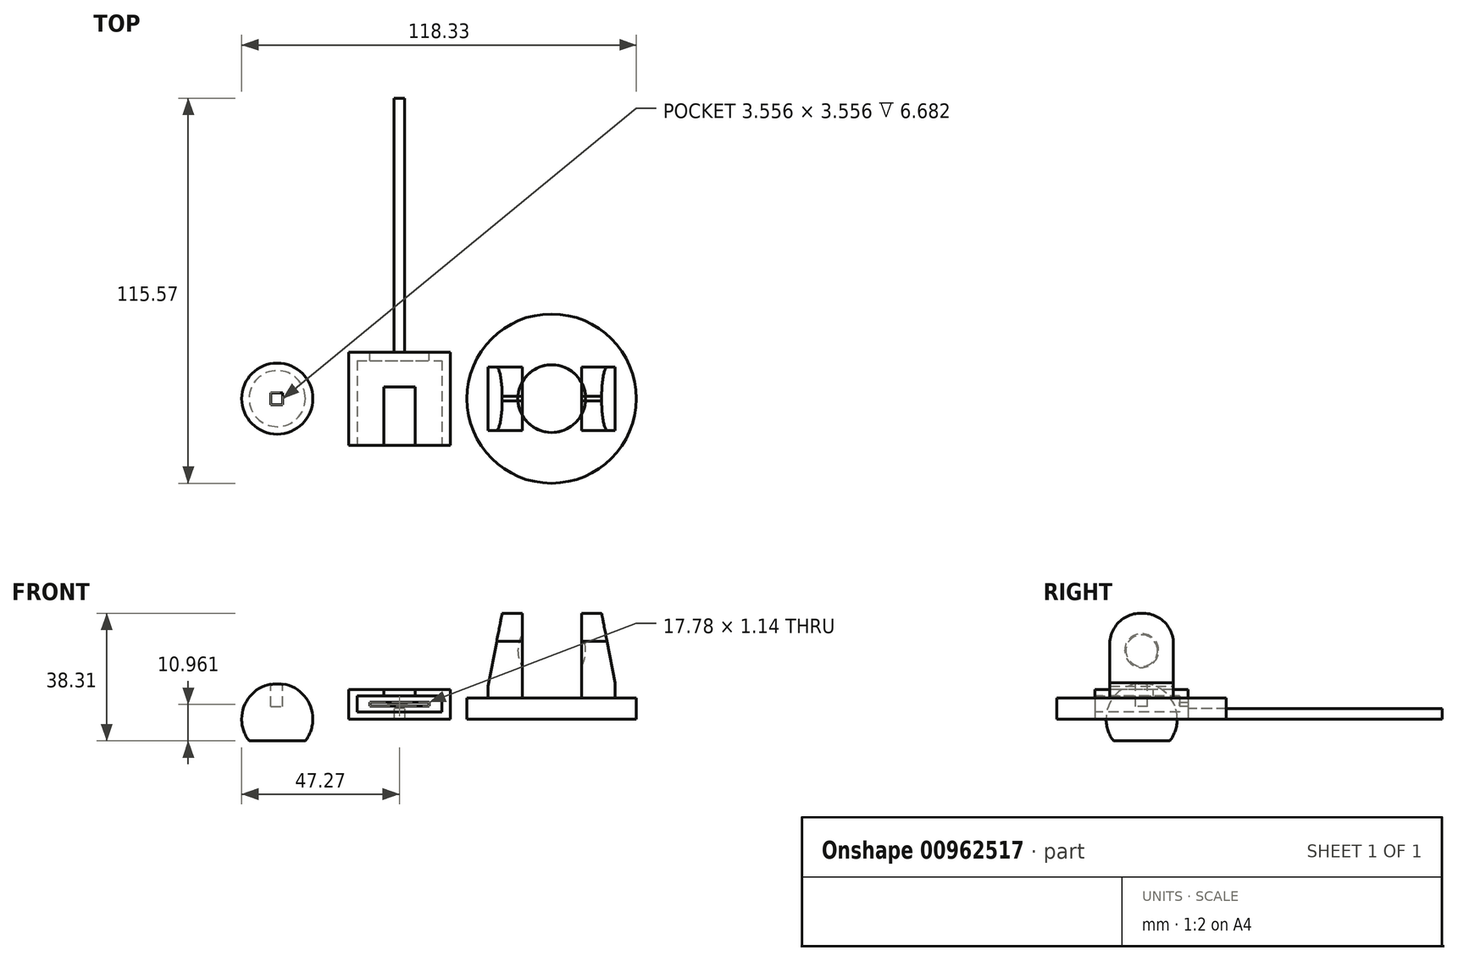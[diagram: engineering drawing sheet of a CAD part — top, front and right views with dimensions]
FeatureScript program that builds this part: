
annotation { "Feature Type Name" : "Feature", "Feature Type Description" : "" }
export const myFeature = defineFeature(function(context is Context, id is Id, definition is map)
    precondition{}
    {
        {
            var Q0;
            Q0=qCreatedBy(makeId("Top.planeOp"),FACE);
            var sketch = newSketch(context, id + "F0", { "sketchPlane" : qUnion([Q0])});
            skLineSegment(sketch, "E0.bottom", {"start": v(-15.24, 13.97) * mm, "end": v(15.24, 13.97) * mm});
            skLineSegment(sketch, "E0.top", {"start": v(-15.24, -13.97) * mm, "end": v(15.24, -13.97) * mm});
            skLineSegment(sketch, "E0.left", {"start": v(-15.24, 13.97) * mm, "end": v(-15.24, -13.97) * mm});
            skLineSegment(sketch, "E0.right", {"start": v(15.24, 13.97) * mm, "end": v(15.24, -13.97) * mm});
            skPoint(sketch, "E0.middle", {"position": v(0, 0) * mm});
            skSolve(sketch);
        }
        {
            var Q0;
            Q0=makeQuery(id+"F0.imprint","IMPRINT",FACE,{"disambiguationData":[TD([[makeQuery(id+"F0.imprint","IMPRINT",EDGE,{"derivedFrom":sQuery(id+"F0.wireOp",EDGE,"E0.bottom")}),-1.0]])]});
            extrude(context, id + "F1", {"entities" : qUnion([Q0]), "depth" : 8.9 * mm, "offsetDistance" : 25.4 * mm});
        }
        {
            var Q0;
            Q0=makeQuery(id+"F1.opExtrude","SWEPT_FACE",FACE,{"disambiguationData":[OSD([sQuery(id+"F0.wireOp",EDGE,"E0.top")])]});
            var sketch = newSketch(context, id + "F2", { "sketchPlane" : qUnion([Q0])});
            skLineSegment(sketch, "E1.bottom", {"start": v(-12.7, 6.9) * mm, "end": v(12.7, 6.9) * mm});
            skLineSegment(sketch, "E1.top", {"start": v(-12.7, 2.07) * mm, "end": v(12.7, 2.07) * mm});
            skLineSegment(sketch, "E1.left", {"start": v(-12.7, 6.9) * mm, "end": v(-12.7, 2.07) * mm});
            skLineSegment(sketch, "E1.right", {"start": v(12.7, 6.9) * mm, "end": v(12.7, 2.07) * mm});
            skPoint(sketch, "E1.middle", {"position": v(0, 4.48) * mm});
            skSolve(sketch);
        }
        {
            var Q0;
            Q0=makeQuery(id+"F2.imprint","IMPRINT",FACE,{"disambiguationData":[TD([[makeQuery(id+"F2.imprint","IMPRINT",EDGE,{"derivedFrom":sQuery(id+"F2.wireOp",EDGE,"E1.bottom")}),-1.0]])]});
            extrude(context, id + "F3", {"entities" : qUnion([Q0]), "operationType" : NewBodyOperationType.REMOVE, "oppositeDirection" : true, "depth" : 25.4 * mm, "offsetDistance" : 25.4 * mm});
        }
        {
            var Q0;
            Q0=makeQuery(id+"F1.opExtrude","SWEPT_FACE",FACE,{"disambiguationData":[OSD([sQuery(id+"F0.wireOp",EDGE,"E0.bottom")])]});
            var sketch = newSketch(context, id + "F4", { "sketchPlane" : qUnion([Q0])});
            skLineSegment(sketch, "E2.bottom", {"start": v(-8.9, 4.97) * mm, "end": v(8.9, 4.97) * mm});
            skLineSegment(sketch, "E2.top", {"start": v(-8.9, 3.83) * mm, "end": v(8.9, 3.83) * mm});
            skLineSegment(sketch, "E2.left", {"start": v(-8.9, 4.97) * mm, "end": v(-8.9, 3.83) * mm});
            skLineSegment(sketch, "E2.right", {"start": v(8.9, 4.97) * mm, "end": v(8.9, 3.83) * mm});
            skPoint(sketch, "E2.middle", {"position": v(0, 4.4) * mm});
            skSolve(sketch);
        }
        {
            var Q0;
            Q0=makeQuery(id+"F4.imprint","IMPRINT",FACE,{"disambiguationData":[TD([[makeQuery(id+"F4.imprint","IMPRINT",EDGE,{"derivedFrom":sQuery(id+"F4.wireOp",EDGE,"E2.bottom")}),-1.0]])]});
            extrude(context, id + "F5", {"entities" : qUnion([Q0]), "operationType" : NewBodyOperationType.REMOVE, "oppositeDirection" : true, "depth" : 6.35 * mm, "offsetDistance" : 25.4 * mm});
        }
        {
            var Q0;
            Q0=makeQuery(id+"F1.opExtrude","CAP_FACE",FACE,{"disambiguationData":[OSD([sQuery(id+"F0.wireOp",EDGE,"E0.bottom"),sQuery(id+"F0.wireOp",EDGE,"E0.top"),sQuery(id+"F0.wireOp",EDGE,"E0.left"),sQuery(id+"F0.wireOp",EDGE,"E0.right")])],"isStart":false});
            var sketch = newSketch(context, id + "F6", { "sketchPlane" : qUnion([Q0])});
            skLineSegment(sketch, "E3.bottom", {"start": v(-4.7, 3.55) * mm, "end": v(4.7, 3.55) * mm});
            skLineSegment(sketch, "E3.top", {"start": v(-4.7, -13.97) * mm, "end": v(4.7, -13.97) * mm});
            skLineSegment(sketch, "E3.left", {"start": v(-4.7, 3.55) * mm, "end": v(-4.7, -13.97) * mm});
            skLineSegment(sketch, "E3.right", {"start": v(4.7, 3.55) * mm, "end": v(4.7, -13.97) * mm});
            skPoint(sketch, "E3.middle", {"position": v(0, -5.2) * mm});
            skPoint(sketch, "E3.middle.positionSnap0", {"position": v(0, -13.97) * mm});
            skPoint(sketch, "E3.centerSnap0", {"position": v(0, -13.97) * mm});
            skSolve(sketch);
        }
        {
            var Q0;
            {var subQ0=sQuery(id+"F6.wireOp",EDGE,"E3.bottom");Q0=makeQuery(id+"F6.imprint","IMPRINT",FACE,{"disambiguationData":[TD([[makeQuery(id+"F6.imprint","IMPRINT",EDGE,{"derivedFrom":subQ0}),-1.0]])]});}
            extrude(context, id + "F7", {"entities" : qUnion([Q0]), "operationType" : NewBodyOperationType.REMOVE, "oppositeDirection" : true, "depth" : 6.35 * mm, "offsetDistance" : 25.4 * mm});
        }
        {
            var Q0;
            Q0=makeQuery(id+"F1.opExtrude","SWEPT_FACE",FACE,{"disambiguationData":[OSD([sQuery(id+"F0.wireOp",EDGE,"E0.bottom")])]});
            var sketch = newSketch(context, id + "F8", { "sketchPlane" : qUnion([Q0])});
            skLineSegment(sketch, "E4.bottom", {"start": v(-1.56, 3.12) * mm, "end": v(1.56, 3.12) * mm});
            skLineSegment(sketch, "E4.top", {"start": v(-1.56, 0) * mm, "end": v(1.56, 0) * mm});
            skLineSegment(sketch, "E4.left", {"start": v(-1.56, 3.12) * mm, "end": v(-1.56, 0) * mm});
            skLineSegment(sketch, "E4.right", {"start": v(1.56, 3.12) * mm, "end": v(1.56, 0) * mm});
            skPoint(sketch, "E4.middle", {"position": v(0, 1.56) * mm});
            skPoint(sketch, "E5", {"position": v(0, 3.83) * mm});
            skSolve(sketch);
        }
        {
            var Q0;
            {var subQ0=sQuery(id+"F8.wireOp",EDGE,"E4.top");Q0=makeQuery(id+"F8.imprint","IMPRINT",FACE,{"disambiguationData":[TD([[makeQuery(id+"F8.imprint","IMPRINT",EDGE,{"derivedFrom":subQ0}),1.0]])]});}
            var Q1;
            Q1=makeQuery(id+"F8.imprint","IMPRINT",FACE,{"disambiguationData":[TD([[makeQuery(id+"F8.imprint","IMPRINT",EDGE,{"derivedFrom":sQuery(id+"F8.wireOp",EDGE,"E4.bottom")}),-1.0]])]});
            extrude(context, id + "F9", {"entities" : qUnion([Q0, Q1]), "operationType" : NewBodyOperationType.ADD, "depth" : 76.2 * mm, "offsetDistance" : 25.4 * mm});
        }
        {
            var Q0;
            Q0=qCreatedBy(makeId("Front.planeOp"),FACE);
            var sketch = newSketch(context, id + "F10", { "sketchPlane" : qUnion([Q0])});
            skArc(sketch, "E6", {"start": v(-25.93, 0) * mm, "mid": v(-36.6, 10.67) * mm, "end": v(-47.27, 0) * mm});
            skLineSegment(sketch, "E7", {"start": v(-47.27, 0) * mm, "end": v(-25.93, 0) * mm});
            skLineSegment(sketch, "E8", {"start": v(-54.4, 0) * mm, "end": v(-21.38, 0) * mm, "construction": true});
            skLineSegment(sketch, "E9", {"start": v(-36.6, 0) * mm, "end": v(-36.6, 46.6) * mm, "construction": true});
            skSolve(sketch);
        }
        {
            var Q0;
            Q0=makeQuery(id+"F10.imprint","IMPRINT",FACE,{"disambiguationData":[TD([[makeQuery(id+"F10.imprint","IMPRINT",EDGE,{"derivedFrom":sQuery(id+"F10.wireOp",EDGE,"E6")}),1.0]])]});
            var Q1;
            Q1=sQuery(id+"F10.wireOp",EDGE,"E8");
            revolve(context, id + "F11", {"surfaceOperationType" : NewSurfaceOperationType.NEW, "entities" : qUnion([Q0]), "axis" : qUnion([Q1]), "revolveType" : RevolveType.FULL});
        }
        {
            var Q0;
            Q0=qCreatedBy(makeId("Front.planeOp"),FACE);
            var Q1;
            Q1 = qBodyType(qCreatedBy(id + "F13" ,EDGE), BodyType.WIRE);
            cPlane(context, id + "F12", {"entities" : qUnion([Q0, Q1]), "cplaneType" : CPlaneType.OFFSET, "offset" : 12.7 * mm, "oppositeDirection" : true, "width" : 152.4 * mm, "height" : 152.4 * mm});
        }
        {
            var Q0;
            Q0=qCreatedBy(id+"F12.planeOp",FACE);
            var sketch = newSketch(context, id + "F13", { "sketchPlane" : qUnion([Q0])});
            skLineSegment(sketch, "E10.bottom", {"start": v(-50.33, -10.92) * mm, "end": v(-23.94, -10.92) * mm});
            skLineSegment(sketch, "E10.top", {"start": v(-50.33, -6.56) * mm, "end": v(-23.94, -6.56) * mm});
            skLineSegment(sketch, "E10.left", {"start": v(-50.33, -10.92) * mm, "end": v(-50.33, -6.56) * mm});
            skLineSegment(sketch, "E10.right", {"start": v(-23.94, -10.92) * mm, "end": v(-23.94, -6.56) * mm});
            skSolve(sketch);
        }
        {
            var Q0;
            Q0=makeQuery(id+"F13.imprint","IMPRINT",FACE,{"disambiguationData":[TD([[makeQuery(id+"F13.imprint","IMPRINT",EDGE,{"derivedFrom":sQuery(id+"F13.wireOp",EDGE,"E10.bottom")}),1.0]])]});
            extrude(context, id + "F14", {"entities" : qUnion([Q0]), "operationType" : NewBodyOperationType.REMOVE, "depth" : 25.4 * mm, "offsetDistance" : 25.4 * mm});
        }
        {
            var Q0;
            Q0=qCreatedBy(makeId("Top.planeOp"),FACE);
            cPlane(context, id + "F15", {"entities" : qUnion([Q0]), "cplaneType" : CPlaneType.OFFSET, "offset" : 12.7 * mm, "width" : 152.4 * mm, "height" : 152.4 * mm});
        }
        {
            var Q0;
            Q0=qCreatedBy(id+"F15.planeOp",FACE);
            var sketch = newSketch(context, id + "F16", { "sketchPlane" : qUnion([Q0])});
            skLineSegment(sketch, "E11.bottom", {"start": v(-38.53, 1.78) * mm, "end": v(-34.97, 1.78) * mm});
            skLineSegment(sketch, "E11.top", {"start": v(-38.53, -1.78) * mm, "end": v(-34.97, -1.78) * mm});
            skLineSegment(sketch, "E11.left", {"start": v(-38.53, 1.78) * mm, "end": v(-38.53, -1.78) * mm});
            skLineSegment(sketch, "E11.right", {"start": v(-34.97, 1.78) * mm, "end": v(-34.97, -1.78) * mm});
            skLineSegment(sketch, "E12", {"start": v(-36.75, 1.78) * mm, "end": v(-36.75, -1.78) * mm, "construction": true});
            skLineSegment(sketch, "E13", {"start": v(-38.53, 0) * mm, "end": v(-34.97, 0) * mm, "construction": true});
            skSolve(sketch);
        }
        {
            var Q0;
            Q0 = qSketchRegion(id + "F16", true);
            extrude(context, id + "F17", {"entities" : qUnion([Q0]), "operationType" : NewBodyOperationType.REMOVE, "oppositeDirection" : true, "depth" : 8.9 * mm, "offsetDistance" : 25.4 * mm});
        }
        {
            var Q0;
            Q0=qCreatedBy(makeId("Top.planeOp"),FACE);
            var sketch = newSketch(context, id + "F18", { "sketchPlane" : qUnion([Q0])});
            skCircle(sketch, "E14", {"center": v(45.66, 0) * mm, "radius": 25.4 * mm});
            skLineSegment(sketch, "E15", {"start": v(45.66, 48.44) * mm, "end": v(45.66, -53.27) * mm, "construction": true});
            skSolve(sketch);
        }
        {
            var Q0;
            Q0=makeQuery(id+"F18.imprint","IMPRINT",FACE,{"disambiguationData":[TD([[makeQuery(id+"F18.imprint","IMPRINT",EDGE,{"derivedFrom":sQuery(id+"F18.wireOp",EDGE,"E14")}),1.0]])]});
            extrude(context, id + "F19", {"entities" : qUnion([Q0]), "depth" : 6.35 * mm, "offsetDistance" : 25.4 * mm});
        }
        {
            var Q0;
            Q0=makeQuery(id+"F19.opExtrude","CAP_FACE",FACE,{"disambiguationData":[OSD([sQuery(id+"F18.wireOp",EDGE,"E14")])],"isStart":false});
            var sketch = newSketch(context, id + "F20", { "sketchPlane" : qUnion([Q0])});
            skLineSegment(sketch, "E16.bottom", {"start": v(26.6, 9.53) * mm, "end": v(64.7, 9.53) * mm});
            skLineSegment(sketch, "E16.top", {"start": v(26.6, -9.53) * mm, "end": v(64.7, -9.53) * mm});
            skLineSegment(sketch, "E16.left", {"start": v(26.6, 9.53) * mm, "end": v(26.6, -9.52) * mm});
            skLineSegment(sketch, "E16.right", {"start": v(64.7, 9.53) * mm, "end": v(64.7, -9.52) * mm});
            skPoint(sketch, "E16.middle", {"position": v(45.66, 0) * mm});
            skSolve(sketch);
        }
        {
            var Q0;
            Q0=makeQuery(id+"F20.imprint","IMPRINT",FACE,{"disambiguationData":[TD([[makeQuery(id+"F20.imprint","IMPRINT",EDGE,{"derivedFrom":sQuery(id+"F20.wireOp",EDGE,"E16.bottom")}),-1.0]])]});
            extrude(context, id + "F21", {"entities" : qUnion([Q0]), "operationType" : NewBodyOperationType.ADD, "depth" : 25.4 * mm, "offsetDistance" : 25.4 * mm});
        }
        {
            var Q0;
            Q0=makeQuery(id+"F21.opExtrude","SWEPT_FACE",FACE,{"disambiguationData":[OSD([sQuery(id+"F20.wireOp",EDGE,"E16.right")])]});
            var sketch = newSketch(context, id + "F22", { "sketchPlane" : qUnion([Q0])});
            skArc(sketch, "E17", {"start": v(0, 31.75) * mm, "mid": v(-6.44, 29.44) * mm, "end": v(-9.52, 23.34) * mm});
            skLineSegment(sketch, "E18", {"start": v(-9.87, 23.34) * mm, "end": v(-9.87, 32.2) * mm});
            skLineSegment(sketch, "E19", {"start": v(-9.87, 32.2) * mm, "end": v(0, 32.55) * mm});
            skLineSegment(sketch, "E20", {"start": v(0, 32.55) * mm, "end": v(0, 31.75) * mm});
            skLineSegment(sketch, "E21", {"start": v(-9.52, 23.34) * mm, "end": v(-9.87, 23.34) * mm});
            skLineSegment(sketch, "E22.MirrorCS", {"start": v(9.87, 32.2) * mm, "end": v(0, 32.55) * mm});
            skArc(sketch, "E23.MirrorCS", {"start": v(0, 31.75) * mm, "mid": v(6.44, 29.44) * mm, "end": v(9.52, 23.34) * mm});
            skLineSegment(sketch, "E24.MirrorCS", {"start": v(9.52, 23.34) * mm, "end": v(9.87, 23.34) * mm});
            skLineSegment(sketch, "E25.MirrorCS", {"start": v(9.87, 23.34) * mm, "end": v(9.87, 32.2) * mm});
            skSolve(sketch);
        }
        {
            var Q0;
            {var subQ0=sQuery(id+"F22.wireOp",EDGE,"E17");var subQ1=sQuery(id+"F20.wireOp",EDGE,"E16.right");var subQ4=makeQuery(id+"F21.opExtrude","CAP_EDGE",EDGE,{"disambiguationData":[OSD([subQ1])],"isStart":false});var subQ5=makeQuery(id+"F22.imprint","INTERSECT",VERTEX,{"derivedFrom":[subQ4,subQ0]});Q0=makeQuery(id+"F22.imprint","IMPRINT",FACE,{"disambiguationData":[TD([[makeQuery(id+"F22.imprint","IMPRINT",EDGE,{"disambiguationData":[TD([[subQ5,-1.0]])],"derivedFrom":subQ4}),1.0]])]});}
            var Q1;
            {var subQ0=sQuery(id+"F22.wireOp",EDGE,"E23.MirrorCS");var subQ1=sQuery(id+"F20.wireOp",EDGE,"E16.right");var subQ4=makeQuery(id+"F21.opExtrude","CAP_EDGE",EDGE,{"disambiguationData":[OSD([subQ1])],"isStart":false});var subQ5=makeQuery(id+"F22.imprint","INTERSECT",VERTEX,{"derivedFrom":[subQ4,subQ0]});Q1=makeQuery(id+"F22.imprint","IMPRINT",FACE,{"disambiguationData":[TD([[makeQuery(id+"F22.imprint","IMPRINT",EDGE,{"disambiguationData":[TD([[subQ5,1.0]])],"derivedFrom":subQ4}),1.0]])]});}
            extrude(context, id + "F23", {"entities" : qUnion([Q0, Q1]), "operationType" : NewBodyOperationType.REMOVE, "oppositeDirection" : true, "depth" : 38.1 * mm, "offsetDistance" : 25.4 * mm});
        }
        {
            var Q0;
            Q0=qCreatedBy(id+"F12.planeOp",FACE);
            var sketch = newSketch(context, id + "F24", { "sketchPlane" : qUnion([Q0])});
            skLineSegment(sketch, "E26.bottom", {"start": v(54.7, 6.35) * mm, "end": v(36.92, 6.35) * mm});
            skLineSegment(sketch, "E26.top", {"start": v(54.7, 31.75) * mm, "end": v(36.92, 31.75) * mm});
            skLineSegment(sketch, "E26.left", {"start": v(54.7, 6.35) * mm, "end": v(54.7, 31.75) * mm});
            skLineSegment(sketch, "E26.right", {"start": v(36.92, 6.35) * mm, "end": v(36.92, 31.75) * mm});
            skSolve(sketch);
        }
        {
            var Q0;
            Q0=makeQuery(id+"F24.imprint","IMPRINT",FACE,{"disambiguationData":[TD([[makeQuery(id+"F24.imprint","IMPRINT",EDGE,{"derivedFrom":sQuery(id+"F24.wireOp",EDGE,"E26.bottom")}),-1.0]])]});
            extrude(context, id + "F25", {"entities" : qUnion([Q0]), "operationType" : NewBodyOperationType.REMOVE, "depth" : 25.4 * mm, "offsetDistance" : 25.4 * mm});
        }
        {
            var Q0;
            Q0=qCreatedBy(id+"F12.planeOp",FACE);
            var sketch = newSketch(context, id + "F26", { "sketchPlane" : qUnion([Q0])});
            skLineSegment(sketch, "E27", {"start": v(31.06, 32.84) * mm, "end": v(26.29, 8.21) * mm});
            skLineSegment(sketch, "E28", {"start": v(26.29, 8.21) * mm, "end": v(26.29, 32.5) * mm});
            skLineSegment(sketch, "E29", {"start": v(26.29, 32.5) * mm, "end": v(31.06, 32.84) * mm});
            skLineSegment(sketch, "E30", {"start": v(45.76, 0) * mm, "end": v(45.76, 46.2) * mm, "construction": true});
            skLineSegment(sketch, "E31.MirrorCS", {"start": v(65.23, 32.5) * mm, "end": v(60.45, 32.84) * mm});
            skLineSegment(sketch, "E32.MirrorCS", {"start": v(60.45, 32.84) * mm, "end": v(65.23, 8.21) * mm});
            skLineSegment(sketch, "E33.MirrorCS", {"start": v(65.23, 8.21) * mm, "end": v(65.23, 32.5) * mm});
            skSolve(sketch);
        }
        {
            var Q0;
            Q0=makeQuery(id+"F26.imprint","IMPRINT",FACE,{"disambiguationData":[TD([[makeQuery(id+"F26.imprint","IMPRINT",EDGE,{"derivedFrom":sQuery(id+"F26.wireOp",EDGE,"E27")}),-1.0]])]});
            var Q1;
            Q1=makeQuery(id+"F26.imprint","IMPRINT",FACE,{"disambiguationData":[TD([[makeQuery(id+"F26.imprint","IMPRINT",EDGE,{"derivedFrom":sQuery(id+"F26.wireOp",EDGE,"E31.MirrorCS")}),1.0]])]});
            extrude(context, id + "F27", {"entities" : qUnion([Q0, Q1]), "operationType" : NewBodyOperationType.REMOVE, "depth" : 50.8 * mm, "offsetDistance" : 25.4 * mm});
        }
        {
            var Q0;
            Q0=qCreatedBy(makeId("Front.planeOp"),FACE);
            var sketch = newSketch(context, id + "F28", { "sketchPlane" : qUnion([Q0])});
            skArc(sketch, "E34", {"start": v(45.76, 10.37) * mm, "mid": v(55.88, 20.57) * mm, "end": v(45.68, 30.69) * mm});
            skLineSegment(sketch, "E35", {"start": v(45.68, 30.69) * mm, "end": v(45.76, 10.37) * mm});
            skLineSegment(sketch, "E36", {"start": v(45.75, 13.32) * mm, "end": v(45.62, 45.27) * mm, "construction": true});
            skSolve(sketch);
        }
        {
            var Q0;
            Q0=makeQuery(id+"F28.imprint","IMPRINT",FACE,{"disambiguationData":[TD([[makeQuery(id+"F28.imprint","IMPRINT",EDGE,{"derivedFrom":sQuery(id+"F28.wireOp",EDGE,"E34")}),1.0]])]});
            var Q1;
            Q1=sQuery(id+"F28.wireOp",EDGE,"E36");
            revolve(context, id + "F29", {"operationType" : NewBodyOperationType.REMOVE, "surfaceOperationType" : NewSurfaceOperationType.NEW, "entities" : qUnion([Q0]), "axis" : qUnion([Q1]), "revolveType" : RevolveType.FULL});
        }
    });
